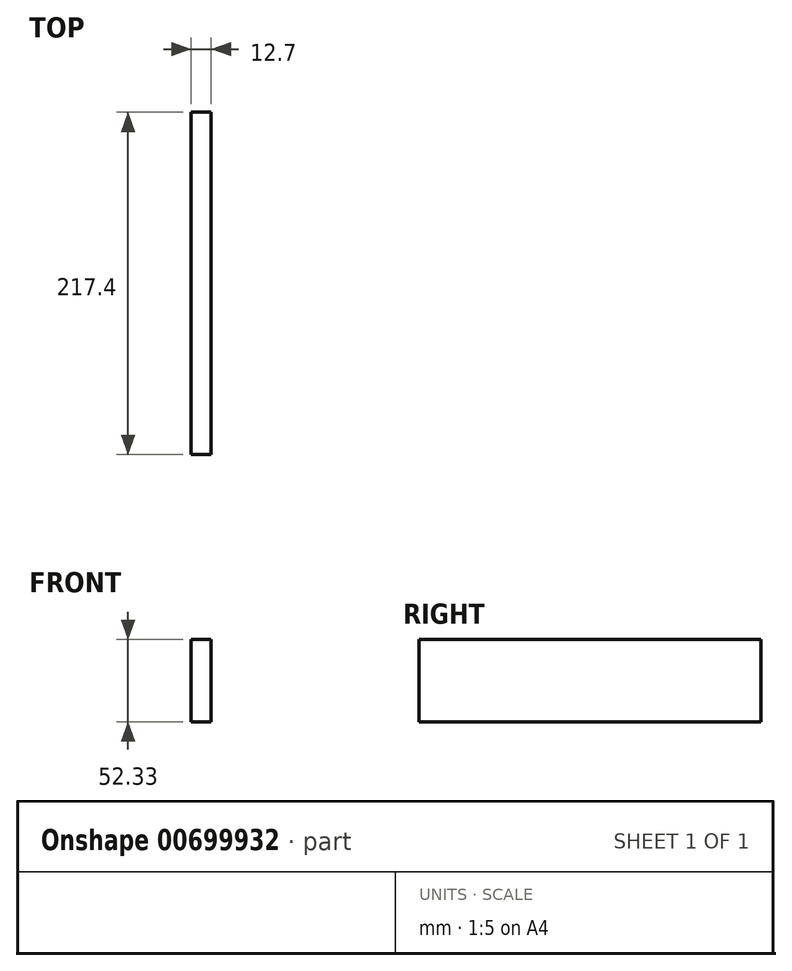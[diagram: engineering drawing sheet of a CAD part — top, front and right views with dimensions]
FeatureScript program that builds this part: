
annotation { "Feature Type Name" : "Feature", "Feature Type Description" : "" }
export const myFeature = defineFeature(function(context is Context, id is Id, definition is map)
    precondition{}
    {
        {
            var Q0;
            Q0=qCreatedBy(makeId("Right.planeOp"),FACE);
            var sketch = newSketch(context, id + "F0", { "sketchPlane" : qUnion([Q0])});
            skLineSegment(sketch, "E0.bottom", {"start": v(-92.65, 41.46) * mm, "end": v(124.75, 41.46) * mm});
            skLineSegment(sketch, "E0.top", {"start": v(-92.65, -10.87) * mm, "end": v(124.75, -10.87) * mm});
            skLineSegment(sketch, "E0.left", {"start": v(-92.65, 41.46) * mm, "end": v(-92.65, -10.87) * mm});
            skLineSegment(sketch, "E0.right", {"start": v(124.75, 41.46) * mm, "end": v(124.75, -10.87) * mm});
            skSolve(sketch);
        }
        {
            var Q0;
            Q0=makeQuery(id+"F0.imprint","IMPRINT",FACE,{"disambiguationData":[TD([[makeQuery(id+"F0.imprint","IMPRINT",EDGE,{"derivedFrom":sQuery(id+"F0.wireOp",EDGE,"E0.bottom")}),-1.0]])]});
            extrude(context, id + "F1", {"entities" : qUnion([Q0]), "depth" : 12.7 * mm, "offsetDistance" : 25.4 * mm});
        }
    });
